# Revit family: TMI - D3800 - Base_3 File Drawers1
name_source: partatom
category: Casework
revit_build: Autodesk Revit 2016 (Build: 20150220_1215(x64)
units: mm (PartAtom-declared; Revit-internal decimal feet)

## family parameters
Always vertical = Yes
Cut with Voids When Loaded = No
OmniClass Number = 23.40.35.14.11
OmniClass Title = Modular Casework
Room Calculation Point = No
Shared = No
Work Plane-Based = No

## types (2) — shared parameters
Cabinet Finish = Plastic Laminate
Casework Back Thickness = 1/4"
Casework Thickness = 3/4"
Countertop Height = 43"
Countertop Thickness = 1 1/4"
Depth = 24"
Distance of Door from Top of Casework = 1/4"
Door Thickness = 3/4"
Height = 41 3/4"
Manufacturer = TMI Systems Corporation
Model = D3800
Toe Kick Depth = 2"
Toe Kick Height = 4"
URL = www.tmisystems.com

## per-type parameters (varying)
| type | Description | Width |
| 16" x 43" x 24" | Base, 3 File Drawers | 16" |
| 19" x 43" x 24" | Base, 3 Legal File Drawers | 19" |

## geometry (parser evidence)
native form markers: Blend x2, Sweep x6
no freeform markers — native parametric forms only
